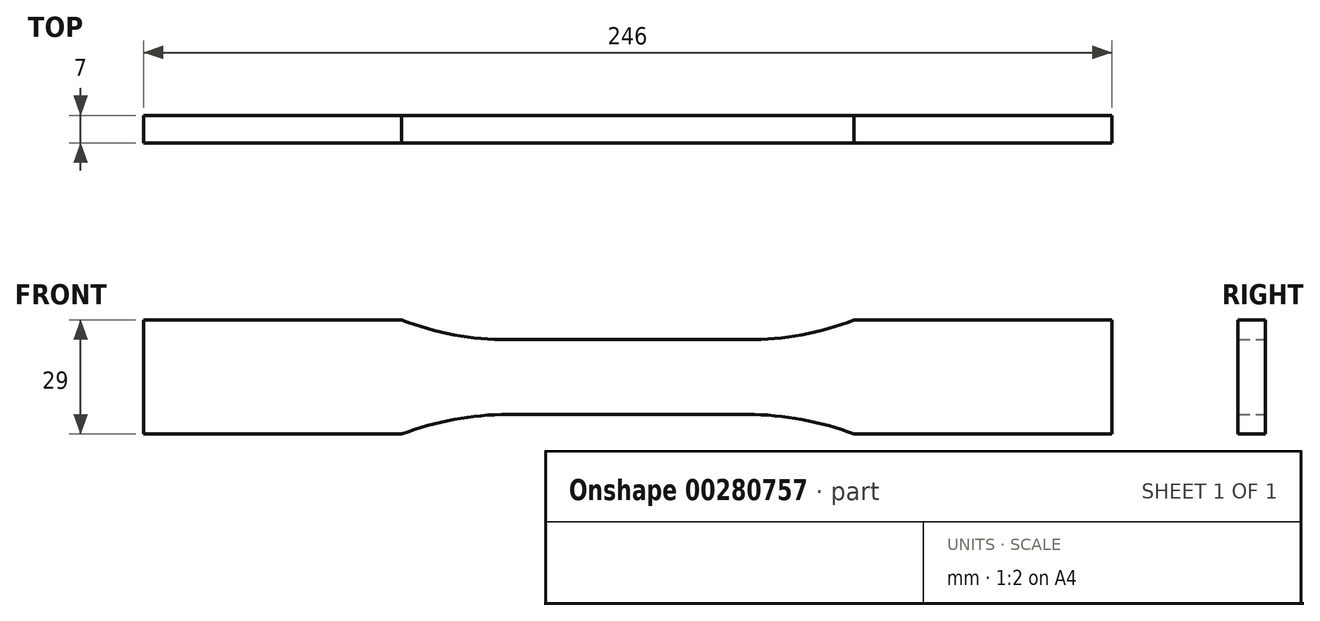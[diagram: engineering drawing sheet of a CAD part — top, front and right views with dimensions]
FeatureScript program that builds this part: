
annotation { "Feature Type Name" : "Feature", "Feature Type Description" : "" }
export const myFeature = defineFeature(function(context is Context, id is Id, definition is map)
    precondition{}
    {
        {
            var Q0;
            Q0=qCreatedBy(makeId("Front.planeOp"),FACE);
            var sketch = newSketch(context, id + "F0", { "sketchPlane" : qUnion([Q0])});
            skLineSegment(sketch, "E0", {"start": v(0, 9.5) * mm, "end": v(30.39, 9.5) * mm});
            skArc(sketch, "E1", {"start": v(30.39, 9.5) * mm, "mid": v(44.17, 10.76) * mm, "end": v(57.5, 14.5) * mm});
            skLineSegment(sketch, "E2", {"start": v(123, 14.5) * mm, "end": v(57.5, 14.5) * mm});
            skLineSegment(sketch, "E3.MirrorCS", {"start": v(123, -14.5) * mm, "end": v(57.5, -14.5) * mm});
            skLineSegment(sketch, "E4.MirrorCS", {"start": v(0, -9.5) * mm, "end": v(30.39, -9.5) * mm});
            skArc(sketch, "E5.MirrorCS", {"start": v(30.39, -9.5) * mm, "mid": v(44.17, -10.76) * mm, "end": v(57.5, -14.5) * mm});
            skArc(sketch, "E6.MirrorCS", {"start": v(-30.39, -9.5) * mm, "mid": v(-44.17, -10.76) * mm, "end": v(-57.5, -14.5) * mm});
            skLineSegment(sketch, "E7.MirrorCS", {"start": v(0, 9.5) * mm, "end": v(-30.39, 9.5) * mm});
            skArc(sketch, "E8.MirrorCS", {"start": v(-30.39, 9.5) * mm, "mid": v(-44.17, 10.76) * mm, "end": v(-57.5, 14.5) * mm});
            skLineSegment(sketch, "E9.MirrorCS", {"start": v(-123, -14.5) * mm, "end": v(-57.5, -14.5) * mm});
            skLineSegment(sketch, "E10.MirrorCS", {"start": v(0, -9.5) * mm, "end": v(-30.39, -9.5) * mm});
            skLineSegment(sketch, "E11.MirrorCS", {"start": v(-123, 14.5) * mm, "end": v(-57.5, 14.5) * mm});
            skLineSegment(sketch, "E12", {"start": v(-123, 14.5) * mm, "end": v(-123, -14.5) * mm});
            skLineSegment(sketch, "E13", {"start": v(123, 14.5) * mm, "end": v(123, -14.5) * mm});
            skSolve(sketch);
        }
        {
            var Q0;
            Q0=makeQuery(id+"F0.imprint","IMPRINT",FACE,{"disambiguationData":[TD([[makeQuery(id+"F0.imprint","IMPRINT",EDGE,{"derivedFrom":sQuery(id+"F0.wireOp",EDGE,"E0")}),-1.0]])]});
            extrude(context, id + "F1", {"entities" : qUnion([Q0]), "endBound" : BoundingType.SYMMETRIC, "depth" : 7 * mm});
        }
    });
